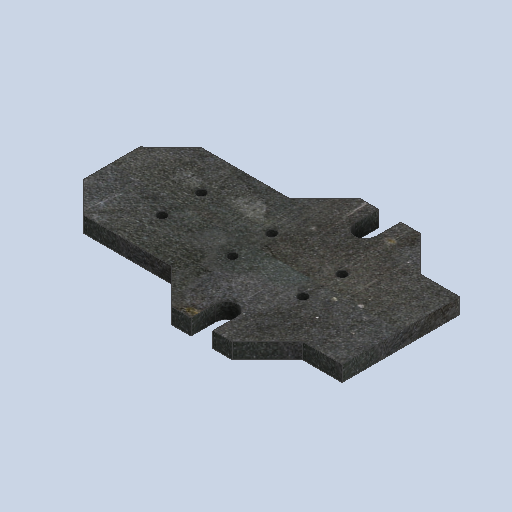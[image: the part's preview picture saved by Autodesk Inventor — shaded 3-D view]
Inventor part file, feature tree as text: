
AUTODESK INVENTOR PART (.ipt)
format: ipt  version: 2023.2 (Build 272271000, 271)  size: 335,872 bytes
history: native  units: mm
features: extrude x2, sketch x2
ambient origin geometry x8: Origin, YZ Plane, XZ Plane, XY Plane, X Axis, Y Axis, Z Axis, Center Point
bodies: Solid1 (feature_tree)
feature tree (4):
  extrude  "Extrusion1"  TaperAngle=135.0deg  [1 undecoded]
  extrude  "Extrusion2"  Depth=185.0mm
  sketch  "Sketch1"  dims[d4=35.0mm d5=135.0deg]
  sketch  "Sketch2"  dims[d7=135.0deg d9=185.0mm d10=75.0mm d19=14.0mm d20=14.0mm d23=67.0mm d24=67.0mm d27=12.5mm d28=15.5mm d29=15.5mm d30=15.5mm d31=15.5mm d32=12.5mm d33=135.0deg d34=12.5mm d35=135.0deg d36=12.5mm d37=45.0deg d38=12.5mm d39=135.0deg d40=11.0mm d41=11.0mm d42=11.0mm d43=11.0mm d44=11.0mm d45=11.0mm d46=50.0mm d47=45.0mm d48=45.0mm d49=25.0mm d51=6.0mm d52=0.0mm d53=14.0mm d55=6.0mm d56=6.0mm d57=6.0mm d58=6.0mm d59=6.0mm d60=6.0mm d61=50.0mm d62=45.0mm d63=45.0mm d64=12.5mm d65=25.0mm d66=4.0mm d67=0.0mm]
note: 1 required parameter value undecoded (feature->parameter linkage not recoverable at this tier; creation-order binding heuristic only, values carry confidence <= 0.55)
